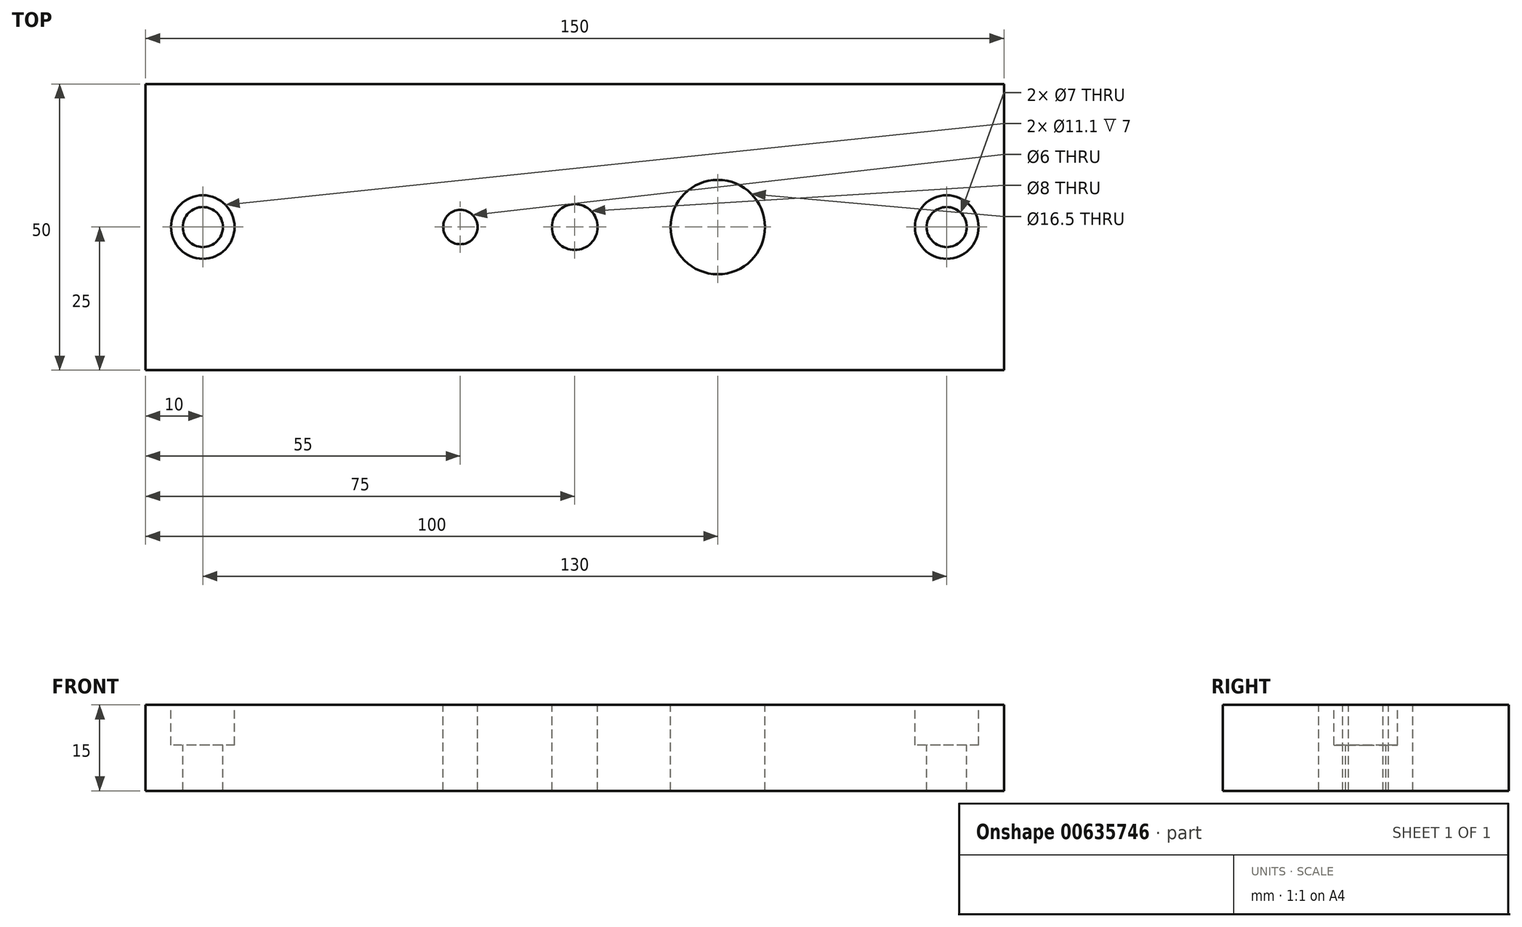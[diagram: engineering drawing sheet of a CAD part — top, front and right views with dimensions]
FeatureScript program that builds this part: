
annotation { "Feature Type Name" : "Feature", "Feature Type Description" : "" }
export const myFeature = defineFeature(function(context is Context, id is Id, definition is map)
    precondition{}
    {
        {
            var Q0;
            Q0=qCreatedBy(makeId("Top.planeOp"),FACE);
            var sketch = newSketch(context, id + "F0", { "sketchPlane" : qUnion([Q0])});
            skLineSegment(sketch, "E0.bottom", {"start": v(0, 0) * mm, "end": v(150, 0) * mm});
            skLineSegment(sketch, "E0.top", {"start": v(0, 50) * mm, "end": v(150, 50) * mm});
            skLineSegment(sketch, "E0.left", {"start": v(0, 0) * mm, "end": v(0, 50) * mm});
            skLineSegment(sketch, "E0.right", {"start": v(150, 0) * mm, "end": v(150, 50) * mm});
            skSolve(sketch);
        }
        {
            var Q0;
            Q0=makeQuery(id+"F0.imprint","IMPRINT",FACE,{"disambiguationData":[TD([[makeQuery(id+"F0.imprint","IMPRINT",EDGE,{"derivedFrom":sQuery(id+"F0.wireOp",EDGE,"E0.bottom")}),1.0]])]});
            extrude(context, id + "F1", {"entities" : qUnion([Q0]), "oppositeDirection" : true, "depth" : 15 * mm, "offsetDistance" : 25 * mm});
        }
        {
            var Q0;
            Q0=makeQuery(id+"F1.opExtrude","CAP_FACE",FACE,{"disambiguationData":[OSD([sQuery(id+"F0.wireOp",EDGE,"E0.bottom"),sQuery(id+"F0.wireOp",EDGE,"E0.top"),sQuery(id+"F0.wireOp",EDGE,"E0.left"),sQuery(id+"F0.wireOp",EDGE,"E0.right")])],"isStart":true});
            var sketch = newSketch(context, id + "F2", { "sketchPlane" : qUnion([Q0])});
            skPoint(sketch, "E1", {"position": v(10, 25) * mm});
            skPoint(sketch, "E2", {"position": v(55, 25) * mm});
            skPoint(sketch, "E3", {"position": v(75, 25) * mm});
            skPoint(sketch, "E4", {"position": v(100, 25) * mm});
            skPoint(sketch, "E5", {"position": v(140, 25) * mm});
            skSolve(sketch);
        }
        {
            var Q0;
            Q0=sQuery(id+"F2.wireOp",VERTEX,"E1");
            var Q1;
            Q1=sQuery(id+"F2.wireOp",VERTEX,"E5");
            var Q2;
            Q2=makeQuery(id+"F1.opExtrude","SWEPT_BODY",BODY,{"disambiguationData":[OSD([sQuery(id+"F0.wireOp",EDGE,"E0.bottom"),sQuery(id+"F0.wireOp",EDGE,"E0.top"),sQuery(id+"F0.wireOp",EDGE,"E0.left"),sQuery(id+"F0.wireOp",EDGE,"E0.right")])]});
            hole(context, id + "F3", {"style" : HoleStyle.C_BORE, "endStyle" : HoleEndStyle.THROUGH, "holeDiameter" : 7 * mm, "cBoreDiameter" : 11.1 * mm, "cBoreDepth" : 7 * mm, "majorDiameter" : 5 * mm, "isTappedThrough" : true, "tappedDepth" : 12.7 * mm, "tapClearance" : 3, "startFromSketch" : true, "locations" : qUnion([Q0, Q1]), "scope" : qUnion([Q2])});
        }
        {
            var Q0;
            Q0=sQuery(id+"F2.wireOp",VERTEX,"E2");
            var Q1;
            Q1=makeQuery(id+"F1.opExtrude","SWEPT_BODY",BODY,{"disambiguationData":[OSD([sQuery(id+"F0.wireOp",EDGE,"E0.bottom"),sQuery(id+"F0.wireOp",EDGE,"E0.top"),sQuery(id+"F0.wireOp",EDGE,"E0.left"),sQuery(id+"F0.wireOp",EDGE,"E0.right")])]});
            hole(context, id + "F4", {"style" : HoleStyle.SIMPLE, "endStyle" : HoleEndStyle.THROUGH, "holeDiameter" : 6 * mm, "majorDiameter" : 5 * mm, "isTappedThrough" : true, "tappedDepth" : 12.7 * mm, "tapClearance" : 3, "startFromSketch" : true, "locations" : qUnion([Q0]), "scope" : qUnion([Q1])});
        }
        {
            var Q0;
            Q0=sQuery(id+"F2.wireOp",VERTEX,"E3");
            var Q1;
            Q1=makeQuery(id+"F1.opExtrude","SWEPT_BODY",BODY,{"disambiguationData":[OSD([sQuery(id+"F0.wireOp",EDGE,"E0.bottom"),sQuery(id+"F0.wireOp",EDGE,"E0.top"),sQuery(id+"F0.wireOp",EDGE,"E0.left"),sQuery(id+"F0.wireOp",EDGE,"E0.right")])]});
            hole(context, id + "F5", {"style" : HoleStyle.SIMPLE, "endStyle" : HoleEndStyle.THROUGH, "holeDiameter" : 8 * mm, "majorDiameter" : 5 * mm, "isTappedThrough" : true, "tappedDepth" : 12.7 * mm, "tapClearance" : 3, "startFromSketch" : true, "locations" : qUnion([Q0]), "scope" : qUnion([Q1])});
        }
        {
            var Q0;
            Q0=sQuery(id+"F2.wireOp",VERTEX,"E4");
            var Q1;
            Q1=makeQuery(id+"F1.opExtrude","SWEPT_BODY",BODY,{"disambiguationData":[OSD([sQuery(id+"F0.wireOp",EDGE,"E0.bottom"),sQuery(id+"F0.wireOp",EDGE,"E0.top"),sQuery(id+"F0.wireOp",EDGE,"E0.left"),sQuery(id+"F0.wireOp",EDGE,"E0.right")])]});
            hole(context, id + "F6", {"style" : HoleStyle.SIMPLE, "endStyle" : HoleEndStyle.THROUGH, "holeDiameter" : 16.5 * mm, "majorDiameter" : 5 * mm, "isTappedThrough" : true, "tappedDepth" : 12.7 * mm, "tapClearance" : 3, "startFromSketch" : true, "locations" : qUnion([Q0]), "scope" : qUnion([Q1])});
        }
    });
